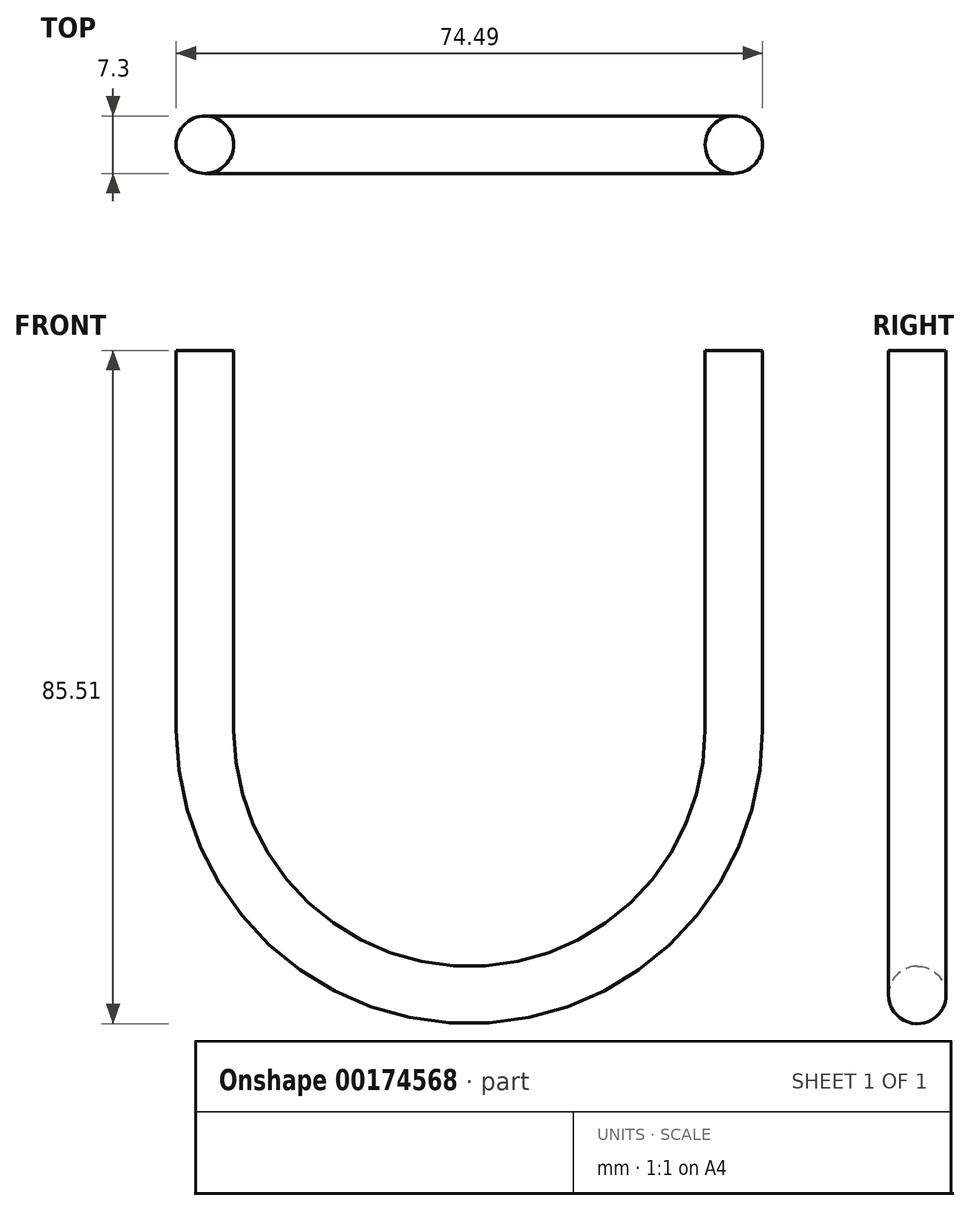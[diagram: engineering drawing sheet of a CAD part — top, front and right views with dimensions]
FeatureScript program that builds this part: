
annotation { "Feature Type Name" : "Feature", "Feature Type Description" : "" }
export const myFeature = defineFeature(function(context is Context, id is Id, definition is map)
    precondition{}
    {
        {
            var Q0;
            Q0=qCreatedBy(makeId("Front.planeOp"),FACE);
            var sketch = newSketch(context, id + "F0", { "sketchPlane" : qUnion([Q0])});
            skLineSegment(sketch, "E0", {"start": v(-34, 0) * mm, "end": v(-34, -48.27) * mm});
            skLineSegment(sketch, "E1", {"start": v(33.13, 0) * mm, "end": v(33.13, -48.27) * mm});
            skArc(sketch, "E2", {"start": v(-34, -48.27) * mm, "mid": v(-0.44, -81.84) * mm, "end": v(33.13, -48.27) * mm});
            skSolve(sketch);
        }
        {
            var Q0;
            Q0=qCreatedBy(makeId("Top.planeOp"),FACE);
            var sketch = newSketch(context, id + "F1", { "sketchPlane" : qUnion([Q0])});
            skCircle(sketch, "E3", {"center": v(-34.04, 0) * mm, "radius": 3.65 * mm});
            skSolve(sketch);
        }
        {
            var Q0;
            Q0=makeQuery(id+"F1.imprint","IMPRINT",FACE,{"disambiguationData":[TD([[makeQuery(id+"F1.imprint","IMPRINT",EDGE,{"derivedFrom":sQuery(id+"F1.wireOp",EDGE,"E3")}),1.0]])]});
            var Q1;
            Q1=sQuery(id+"F0.wireOp",EDGE,"E0");
            var Q2;
            Q2=sQuery(id+"F0.wireOp",EDGE,"E2");
            var Q3;
            Q3=sQuery(id+"F0.wireOp",EDGE,"E1");
            sweep(context, id + "F2", {"profiles" : qUnion([Q0]), "path" : qUnion([Q1, Q2, Q3])});
        }
    });
